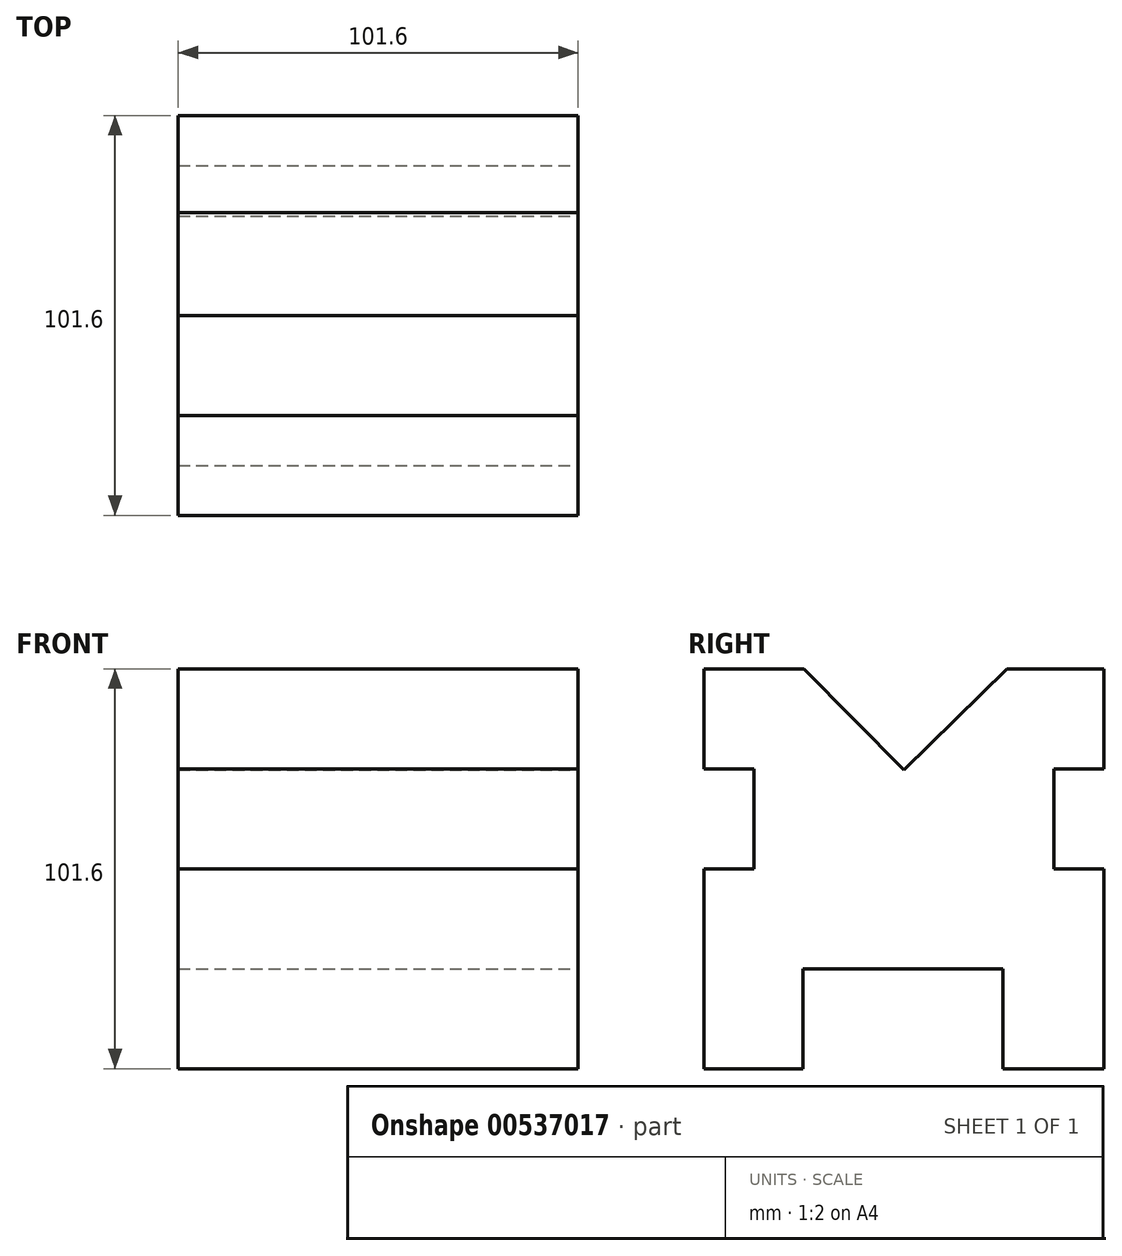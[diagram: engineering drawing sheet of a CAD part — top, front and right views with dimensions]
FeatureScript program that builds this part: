
annotation { "Feature Type Name" : "Feature", "Feature Type Description" : "" }
export const myFeature = defineFeature(function(context is Context, id is Id, definition is map)
    precondition{}
    {
        {
            var Q0;
            Q0=qCreatedBy(makeId("Top.planeOp"),FACE);
            var sketch = newSketch(context, id + "F0", { "sketchPlane" : qUnion([Q0])});
            skLineSegment(sketch, "E0.bottom", {"start": v(0, 0) * mm, "end": v(-101.6, 0) * mm});
            skLineSegment(sketch, "E0.top", {"start": v(0, -101.6) * mm, "end": v(-101.6, -101.6) * mm});
            skLineSegment(sketch, "E0.left", {"start": v(0, 0) * mm, "end": v(0, -101.6) * mm});
            skLineSegment(sketch, "E0.right", {"start": v(-101.6, 0) * mm, "end": v(-101.6, -101.6) * mm});
            skSolve(sketch);
        }
        {
            var Q0;
            Q0=qSketchRegion(id+"F0",true);
            extrude(context, id + "F1", {"entities" : qUnion([Q0]), "depth" : 101.6 * mm, "offsetDistance" : 25.4 * mm});
        }
        {
            var Q0;
            Q0=makeQuery(id+"F1.opExtrude","SWEPT_FACE",FACE,{"disambiguationData":[OSD([sQuery(id+"F0.wireOp",EDGE,"E0.left")])]});
            var sketch = newSketch(context, id + "F2", { "sketchPlane" : qUnion([Q0])});
            skLineSegment(sketch, "E1", {"start": v(-101.6, 50.8) * mm, "end": v(-88.9, 50.8) * mm});
            skLineSegment(sketch, "E2", {"start": v(-88.9, 50.8) * mm, "end": v(-88.9, 76.2) * mm});
            skLineSegment(sketch, "E3", {"start": v(-88.9, 76.2) * mm, "end": v(-101.6, 76.2) * mm});
            skLineSegment(sketch, "E4", {"start": v(-101.6, 101.6) * mm, "end": v(-76.2, 101.6) * mm});
            skLineSegment(sketch, "E5", {"start": v(-50.8, 101.6) * mm, "end": v(-50.8, 0) * mm});
            skLineSegment(sketch, "E6", {"start": v(-76.2, 101.6) * mm, "end": v(-50.8, 75.86) * mm});
            skLineSegment(sketch, "E7", {"start": v(-50.8, 75.86) * mm, "end": v(-24.7, 101.6) * mm});
            skLineSegment(sketch, "E8", {"start": v(0, 50.8) * mm, "end": v(-12.7, 50.8) * mm});
            skLineSegment(sketch, "E9", {"start": v(-12.7, 50.8) * mm, "end": v(-12.7, 76.2) * mm});
            skLineSegment(sketch, "E10", {"start": v(-12.7, 76.2) * mm, "end": v(0, 76.2) * mm});
            skLineSegment(sketch, "E11", {"start": v(-76.44, 0) * mm, "end": v(-76.44, 25.4) * mm});
            skLineSegment(sketch, "E12", {"start": v(-76.44, 25.4) * mm, "end": v(-25.64, 25.4) * mm});
            skLineSegment(sketch, "E13", {"start": v(-25.64, 25.4) * mm, "end": v(-25.64, 0) * mm});
            skSolve(sketch);
        }
        {
            var Q0;
            Q0=qSketchRegion(id+"F2",true);
            var Q1;
            {var subQ3=sQuery(id+"F2.wireOp",EDGE,"E6");Q1=makeQuery(id+"F2.imprint","IMPRINT",FACE,{"disambiguationData":[TD([[makeQuery(id+"F2.imprint","IMPRINT",EDGE,{"derivedFrom":subQ3}),1.0]])]});}
            var Q2;
            {var subQ3=sQuery(id+"F2.wireOp",EDGE,"E7");Q2=makeQuery(id+"F2.imprint","IMPRINT",FACE,{"disambiguationData":[TD([[makeQuery(id+"F2.imprint","IMPRINT",EDGE,{"derivedFrom":subQ3}),1.0]])]});}
            var Q3;
            {var subQ0=sQuery(id+"F2.wireOp",EDGE,"E1");Q3=makeQuery(id+"F2.imprint","IMPRINT",FACE,{"disambiguationData":[TD([[makeQuery(id+"F2.imprint","IMPRINT",EDGE,{"derivedFrom":subQ0}),1.0]])]});}
            var Q4;
            {var subQ5=sQuery(id+"F2.wireOp",EDGE,"E11");Q4=makeQuery(id+"F2.imprint","IMPRINT",FACE,{"disambiguationData":[TD([[makeQuery(id+"F2.imprint","IMPRINT",EDGE,{"derivedFrom":subQ5}),-1.0]])]});}
            var Q5;
            {var subQ5=sQuery(id+"F2.wireOp",EDGE,"E13");Q5=makeQuery(id+"F2.imprint","IMPRINT",FACE,{"disambiguationData":[TD([[makeQuery(id+"F2.imprint","IMPRINT",EDGE,{"derivedFrom":subQ5}),-1.0]])]});}
            var Q6;
            {var subQ0=sQuery(id+"F2.wireOp",EDGE,"E8");Q6=makeQuery(id+"F2.imprint","IMPRINT",FACE,{"disambiguationData":[TD([[makeQuery(id+"F2.imprint","IMPRINT",EDGE,{"derivedFrom":subQ0}),-1.0]])]});}
            extrude(context, id + "F3", {"entities" : qUnion([Q0, Q1, Q2, Q3, Q4, Q5, Q6]), "operationType" : NewBodyOperationType.REMOVE, "oppositeDirection" : true, "depth" : 101.6 * mm, "offsetDistance" : 25.4 * mm});
        }
    });
